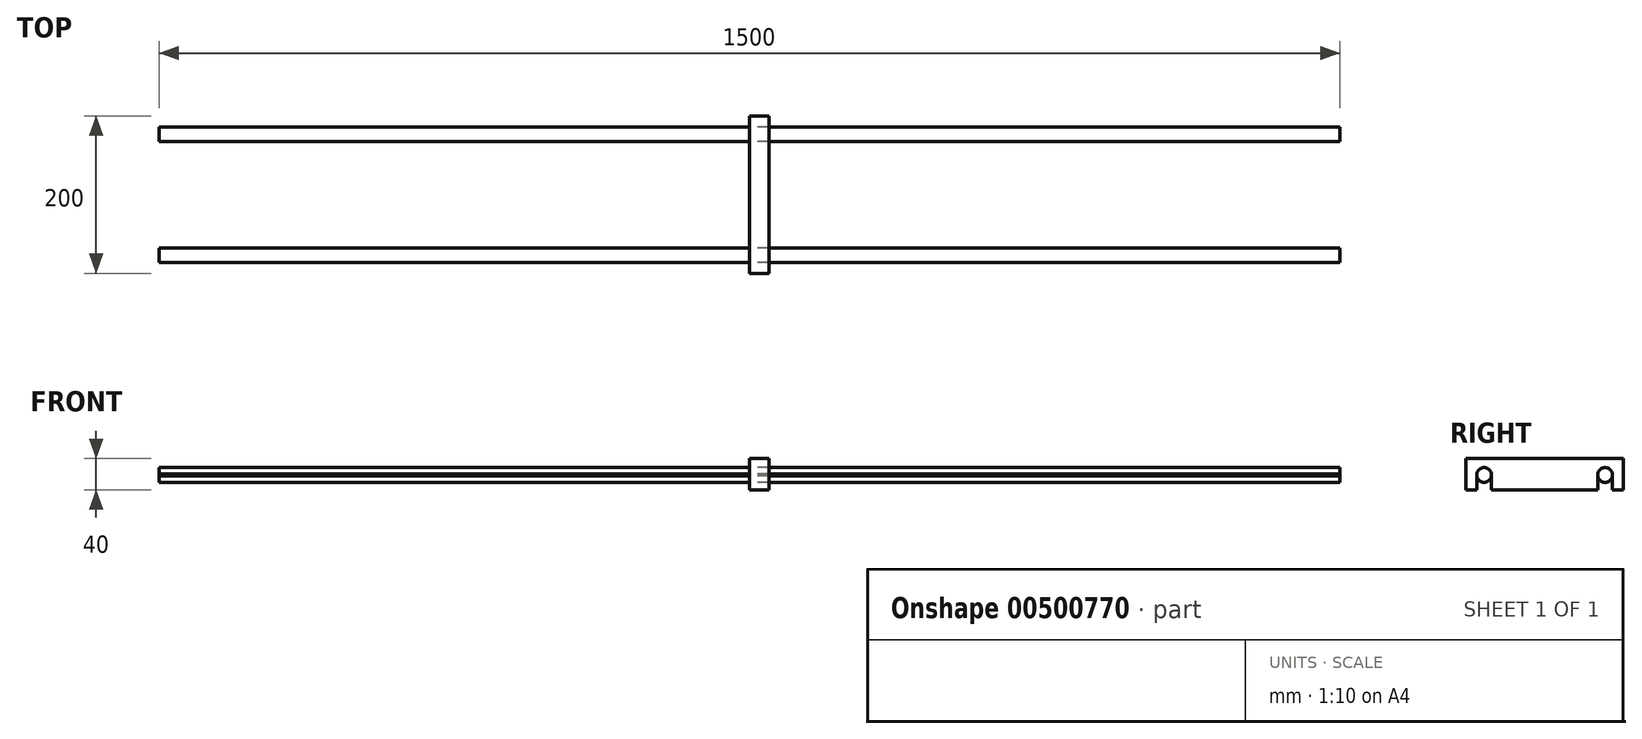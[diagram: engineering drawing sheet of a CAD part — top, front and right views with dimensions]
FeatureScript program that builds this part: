
annotation { "Feature Type Name" : "Feature", "Feature Type Description" : "" }
export const myFeature = defineFeature(function(context is Context, id is Id, definition is map)
    precondition{}
    {
        {
            var Q0;
            Q0=qCreatedBy(makeId("Right.planeOp"),FACE);
            var sketch = newSketch(context, id + "F0", { "sketchPlane" : qUnion([Q0])});
            skLineSegment(sketch, "E0.bottom", {"start": v(-95.64, -0.3) * mm, "end": v(104.36, -0.3) * mm});
            skLineSegment(sketch, "E0.top", {"start": v(-95.64, -40.3) * mm, "end": v(104.36, -40.3) * mm});
            skLineSegment(sketch, "E0.left", {"start": v(-95.64, -0.3) * mm, "end": v(-95.64, -40.3) * mm});
            skLineSegment(sketch, "E0.right", {"start": v(104.36, -0.3) * mm, "end": v(104.36, -40.3) * mm});
            skCircle(sketch, "E1", {"center": v(-72.49, -21.33) * mm, "radius": 9.4 * mm});
            skCircle(sketch, "E2", {"center": v(81.21, -21.33) * mm, "radius": 9.4 * mm});
            skLineSegment(sketch, "E3", {"start": v(-63.09, -21.33) * mm, "end": v(-63.09, -40.3) * mm});
            skLineSegment(sketch, "E4", {"start": v(-81.83, -20.3) * mm, "end": v(-81.83, -40.3) * mm});
            skPoint(sketch, "E4.startSnap0", {"position": v(-95.64, -20.3) * mm});
            skLineSegment(sketch, "E5", {"start": v(71.81, -21.33) * mm, "end": v(71.81, -40.3) * mm});
            skLineSegment(sketch, "E6", {"start": v(90.61, -21.37) * mm, "end": v(90.61, -40.3) * mm});
            skSolve(sketch);
        }
        {
            var Q0;
            Q0=makeQuery(id+"F0.imprint","IMPRINT",FACE,{"disambiguationData":[TD([[makeQuery(id+"F0.imprint","IMPRINT",EDGE,{"derivedFrom":sQuery(id+"F0.wireOp",EDGE,"E0.bottom")}),-1.0]])]});
            extrude(context, id + "F1", {"entities" : qUnion([Q0]), "depth" : 25 * mm});
        }
        {
            var Q0;
            {var subQ0=sQuery(id+"F0.wireOp",EDGE,"E2");var subQ1=makeQuery(id+"F0.imprint","INTERSECT",VERTEX,{"derivedFrom":[subQ0,sQuery(id+"F0.wireOp",EDGE,"E5")]});Q0=makeQuery(id+"F0.imprint","IMPRINT",FACE,{"disambiguationData":[TD([[makeQuery(id+"F0.imprint","IMPRINT",EDGE,{"disambiguationData":[TD([[subQ1,-1.0]])],"derivedFrom":subQ0}),1.0]])]});}
            var Q1;
            {var subQ0=sQuery(id+"F0.wireOp",EDGE,"E1");var subQ1=makeQuery(id+"F0.imprint","INTERSECT",VERTEX,{"derivedFrom":[subQ0,sQuery(id+"F0.wireOp",EDGE,"E3")]});Q1=makeQuery(id+"F0.imprint","IMPRINT",FACE,{"disambiguationData":[TD([[makeQuery(id+"F0.imprint","IMPRINT",EDGE,{"disambiguationData":[TD([[subQ1,-1.0]])],"derivedFrom":subQ0}),1.0]])]});}
            extrude(context, id + "F2", {"entities" : qUnion([Q0, Q1]), "endBound" : BoundingType.SYMMETRIC, "depth" : 1500 * mm});
        }
    });
